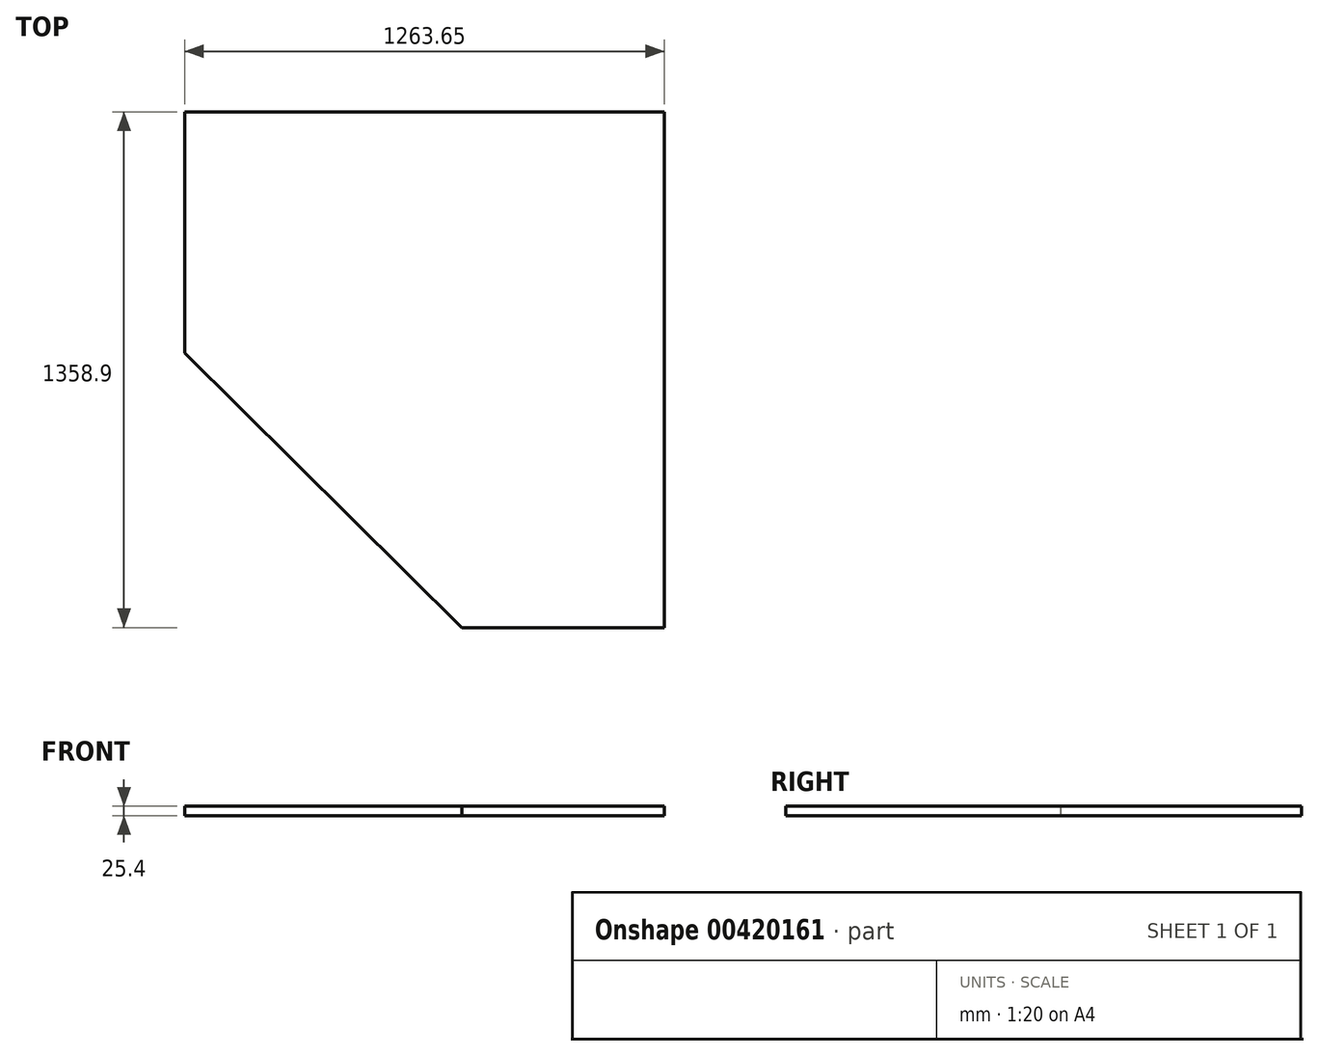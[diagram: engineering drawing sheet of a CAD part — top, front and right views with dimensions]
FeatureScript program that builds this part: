
annotation { "Feature Type Name" : "Feature", "Feature Type Description" : "" }
export const myFeature = defineFeature(function(context is Context, id is Id, definition is map)
    precondition{}
    {
        {
            var Q0;
            Q0=qCreatedBy(makeId("Top.planeOp"),FACE);
            var sketch = newSketch(context, id + "F0", { "sketchPlane" : qUnion([Q0])});
            skLineSegment(sketch, "E0", {"start": v(0, 0) * mm, "end": v(-1263.65, 0) * mm});
            skLineSegment(sketch, "E1", {"start": v(-1263.65, 0) * mm, "end": v(-1263.65, -635) * mm});
            skLineSegment(sketch, "E2", {"start": v(-1263.65, -635) * mm, "end": v(-533.4, -1358.9) * mm});
            skLineSegment(sketch, "E3", {"start": v(-533.4, -1358.9) * mm, "end": v(0, -1358.9) * mm});
            skLineSegment(sketch, "E4", {"start": v(0, -1358.9) * mm, "end": v(0, 0) * mm});
            skSolve(sketch);
        }
        {
            var Q0;
            Q0 = qSketchRegion(id + "F0", true);
            extrude(context, id + "F1", {"entities" : qUnion([Q0]), "depth" : 25.4 * mm});
        }
    });
